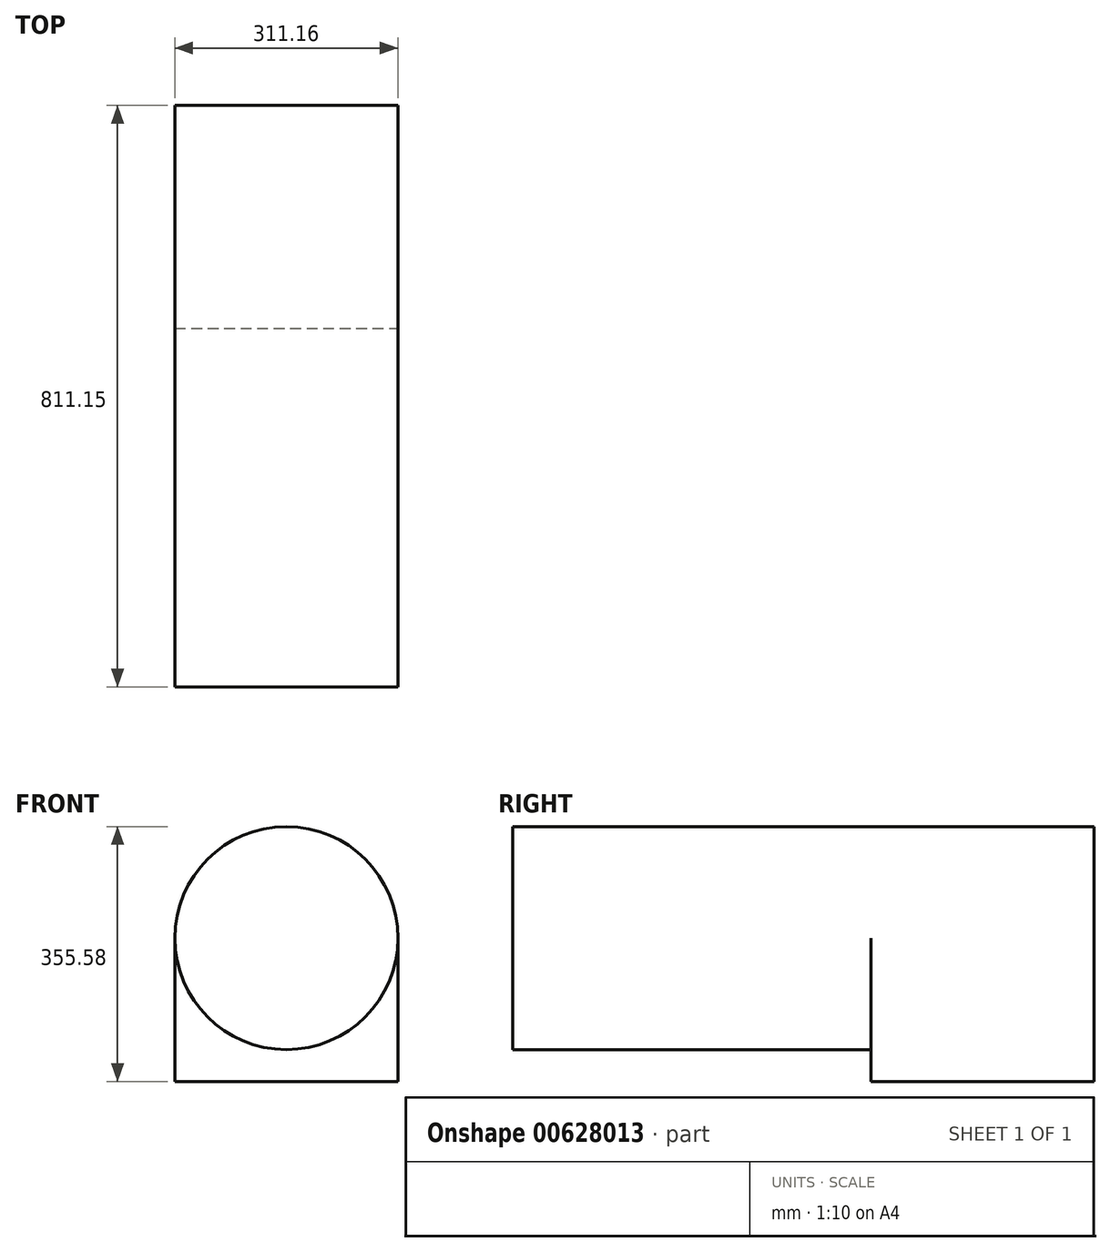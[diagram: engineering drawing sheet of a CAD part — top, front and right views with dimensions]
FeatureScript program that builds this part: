
annotation { "Feature Type Name" : "Feature", "Feature Type Description" : "" }
export const myFeature = defineFeature(function(context is Context, id is Id, definition is map)
    precondition{}
    {
        {
            var Q0;
            Q0=qCreatedBy(makeId("Front.planeOp"),FACE);
            var sketch = newSketch(context, id + "F0", { "sketchPlane" : qUnion([Q0])});
            skCircle(sketch, "E0", {"center": v(0, 0) * mm, "radius": 155.57 * mm});
            skLineSegment(sketch, "E1", {"start": v(-155.57, 0) * mm, "end": v(-155.57, -200) * mm});
            skLineSegment(sketch, "E2", {"start": v(-155.57, -200) * mm, "end": v(155.58, -200) * mm});
            skLineSegment(sketch, "E3", {"start": v(155.57, -200) * mm, "end": v(155.57, 0) * mm});
            skSolve(sketch);
        }
        {
            var Q0;
            {var subQ0=sQuery(id+"F0.wireOp",EDGE,"E0");var subQ1=makeQuery(id+"F0.imprint","INTERSECT",VERTEX,{"derivedFrom":[subQ0,sQuery(id+"F0.wireOp",EDGE,"E1")]});Q0=makeQuery(id+"F0.imprint","IMPRINT",FACE,{"disambiguationData":[TD([[makeQuery(id+"F0.imprint","IMPRINT",EDGE,{"disambiguationData":[TD([[subQ1,-1.0]])],"derivedFrom":subQ0}),1.0]])]});}
            extrude(context, id + "F1", {"entities" : qUnion([Q0]), "depth" : 500 * mm, "offsetDistance" : 25 * mm});
        }
        {
            var Q0;
            Q0 = qSketchRegion(id + "F0", true);
            extrude(context, id + "F2", {"entities" : qUnion([Q0]), "operationType" : NewBodyOperationType.ADD, "oppositeDirection" : true, "depth" : 311.15 * mm, "offsetDistance" : 25 * mm});
        }
    });
